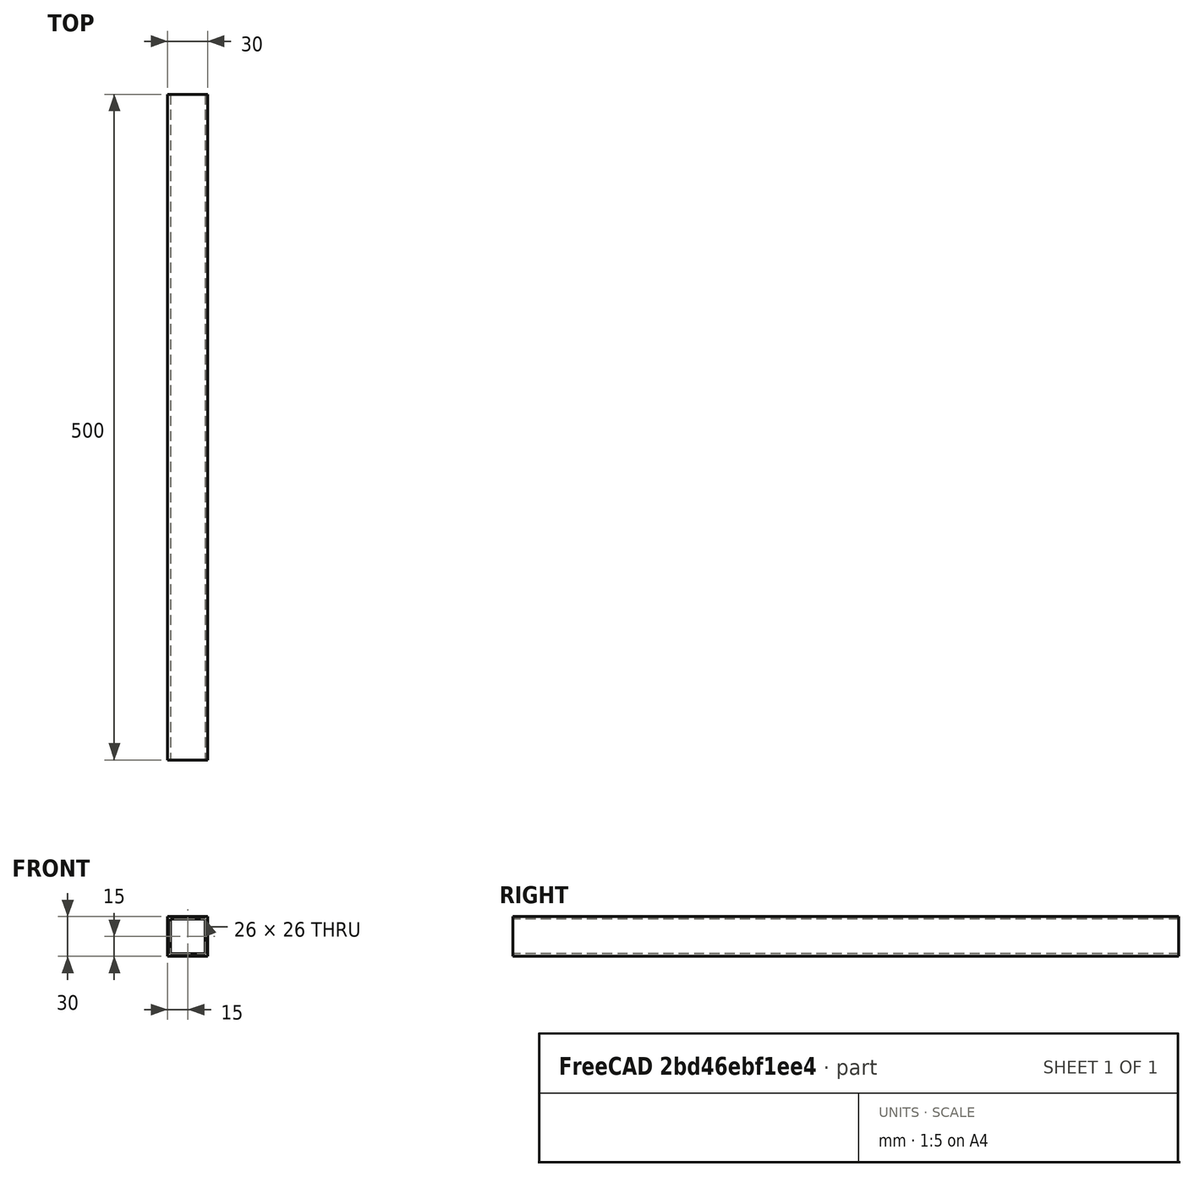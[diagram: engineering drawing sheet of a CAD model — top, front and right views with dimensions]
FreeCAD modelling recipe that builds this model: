
FCSTD DOCUMENT  (FreeCAD 0.20R29177 +426 (Git))
Label: beam_cross_bottom_front
License: All rights reserved
LicenseURL: http://en.wikipedia.org/wiki/All_rights_reserved
objects: Sketcher::SketchObject×1, PartDesign::Pad×1, PartDesign::Body×1
note: 4 computed .brp shape members not serialized (recipe doc carries the construction recipe); baked Part::Feature solids carry a one-line shape summary decoded from their .brp

FEATURE [Sketcher::SketchObject] Sketch
  FullyConstrained = true
  MapMode = 5
  Placement = pos=(0,0,0) rot=(1,0,0;1.5708rad)
  Support = -> [XZ_Plane]
  sketch-geometry (10):
    g0: LineSegment StartX=0 StartY=0 StartZ=0 EndX=30 EndY=0 EndZ=0
    g1: LineSegment StartX=30 StartY=0 StartZ=0 EndX=30 EndY=30 EndZ=0
    g2: LineSegment StartX=30 StartY=30 StartZ=0 EndX=0 EndY=30 EndZ=0
    g3: LineSegment StartX=0 StartY=30 StartZ=0 EndX=0 EndY=0 EndZ=0
    g4: LineSegment StartX=2 StartY=28 StartZ=0 EndX=28 EndY=28 EndZ=0
    g5: LineSegment StartX=28 StartY=28 StartZ=0 EndX=28 EndY=2 EndZ=0
    g6: LineSegment StartX=28 StartY=2 StartZ=0 EndX=2 EndY=2 EndZ=0
    g7: LineSegment StartX=2 StartY=2 StartZ=0 EndX=2 EndY=28 EndZ=0
    g8: LineSegment StartX=0 StartY=0 StartZ=0 EndX=30 EndY=30 EndZ=0
    g9: LineSegment StartX=0 StartY=30 StartZ=0 EndX=30 EndY=0 EndZ=0
  constraints (27):
    c: Coincident(g0,g1)
    c: Coincident(g1,g2)
    c: Coincident(g2,g3)
    c: Coincident(g3,g0)
    c: Horizontal(g0)
    c: Horizontal(g2)
    c: Vertical(g1)
    c: Vertical(g3)
    c: Coincident(g0,g-1)
    c: DistanceX(g2,g2) = 30
    c: Coincident(g4,g5)
    c: Coincident(g5,g6)
    c: Coincident(g6,g7)
    c: Coincident(g7,g4)
    c: Horizontal(g4)
    c: Horizontal(g6)
    c: Vertical(g5)
    c: Vertical(g7)
    c: DistanceY(g4,g1) = 2
    c: Equal(g1,g2)
    c: Equal(g4,g5)
    c: Coincident(g8,g0)
    c: Coincident(g8,g1)
    c: PointOnObject(g4,g8)
    c: Coincident(g9,g2)
    c: Coincident(g9,g0)
    c: PointOnObject(g4,g9)
FEATURE [PartDesign::Pad] Pad
  Direction = (0,-1,-2e-16)
  Length = 500
  Length2 = 10
  Placement = pos=(0,0,0) rot=(1,0,0;1.5708rad)
  Profile = -> Sketch
  ReferenceAxis = -> Sketch [N_Axis]
  Refine = true
  Type = 0
FEATURE [PartDesign::Body] Body
  Group = -> [Sketch,Pad]
  Origin = -> Origin
  Tip = -> Pad
